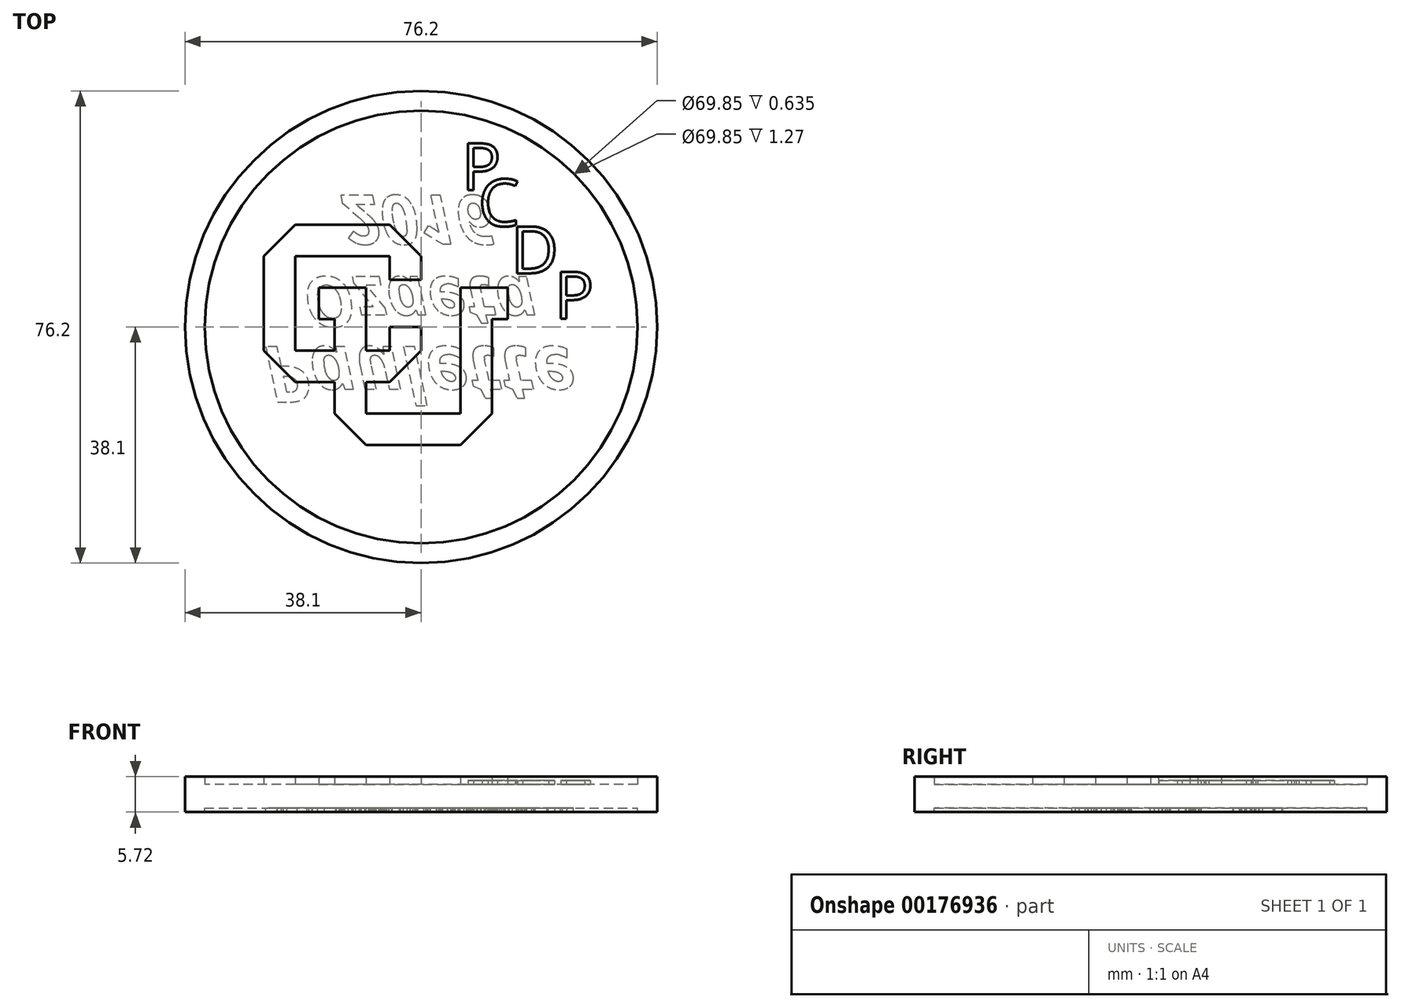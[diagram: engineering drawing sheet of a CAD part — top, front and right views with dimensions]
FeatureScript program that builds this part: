
annotation { "Feature Type Name" : "Feature", "Feature Type Description" : "" }
export const myFeature = defineFeature(function(context is Context, id is Id, definition is map)
    precondition{}
    {
        {
            var Q0;
            Q0=qCreatedBy(makeId("Top.planeOp"),FACE);
            var sketch = newSketch(context, id + "F0", { "sketchPlane" : qUnion([Q0])});
            skCircle(sketch, "E0", {"center": v(0, 0) * mm, "radius": 38.1 * mm});
            skSolve(sketch);
        }
        {
            var Q0;
            Q0=qCreatedBy(makeId("Top.planeOp"),FACE);
            var sketch = newSketch(context, id + "F1", { "sketchPlane" : qUnion([Q0])});
            skCircle(sketch, "E1", {"center": v(0, 0) * mm, "radius": 38.1 * mm});
            skLineSegment(sketch, "E2", {"start": v(0, 0) * mm, "end": v(0, -3.81) * mm});
            skLineSegment(sketch, "E3", {"start": v(0, -3.81) * mm, "end": v(-5.08, -8.9) * mm});
            skLineSegment(sketch, "E4", {"start": v(-5.08, -8.9) * mm, "end": v(-8.89, -8.9) * mm});
            skLineSegment(sketch, "E5", {"start": v(-20.32, -8.9) * mm, "end": v(-25.4, -3.81) * mm});
            skLineSegment(sketch, "E6", {"start": v(-25.4, -3.81) * mm, "end": v(-25.4, 11.43) * mm});
            skLineSegment(sketch, "E7", {"start": v(-25.4, 11.43) * mm, "end": v(-20.32, 16.5) * mm});
            skLineSegment(sketch, "E8", {"start": v(-20.32, 16.5) * mm, "end": v(-5.08, 16.5) * mm});
            skLineSegment(sketch, "E9", {"start": v(-5.08, 16.5) * mm, "end": v(0, 11.43) * mm});
            skLineSegment(sketch, "E10", {"start": v(0, 11.43) * mm, "end": v(0, 7.62) * mm});
            skLineSegment(sketch, "E11", {"start": v(0, 7.62) * mm, "end": v(-5.08, 7.62) * mm});
            skLineSegment(sketch, "E12", {"start": v(-5.08, 7.62) * mm, "end": v(-5.08, 11.43) * mm});
            skLineSegment(sketch, "E13", {"start": v(-5.08, 11.43) * mm, "end": v(-20.32, 11.43) * mm});
            skLineSegment(sketch, "E14", {"start": v(-20.32, 11.43) * mm, "end": v(-20.32, -3.81) * mm});
            skLineSegment(sketch, "E15", {"start": v(-20.32, -3.81) * mm, "end": v(-13.97, -3.81) * mm});
            skLineSegment(sketch, "E16", {"start": v(-5.08, -3.81) * mm, "end": v(-5.08, 0) * mm});
            skLineSegment(sketch, "E17", {"start": v(-5.08, 0) * mm, "end": v(0, 0) * mm});
            skLineSegment(sketch, "E18", {"start": v(-8.89, -3.81) * mm, "end": v(-8.89, 6.35) * mm});
            skLineSegment(sketch, "E19", {"start": v(-8.89, 6.35) * mm, "end": v(-16.51, 6.35) * mm});
            skLineSegment(sketch, "E20", {"start": v(-16.51, 6.35) * mm, "end": v(-16.51, 1.27) * mm});
            skLineSegment(sketch, "E21", {"start": v(-16.51, 1.27) * mm, "end": v(-13.97, 1.27) * mm});
            skLineSegment(sketch, "E22", {"start": v(-13.97, 1.27) * mm, "end": v(-13.97, -3.81) * mm});
            skLineSegment(sketch, "E23.trimOffspring", {"start": v(-8.89, -3.81) * mm, "end": v(-5.08, -3.81) * mm});
            skLineSegment(sketch, "E24", {"start": v(-13.97, -8.9) * mm, "end": v(-13.97, -13.97) * mm});
            skLineSegment(sketch, "E25", {"start": v(-13.97, -13.97) * mm, "end": v(-8.89, -19.05) * mm});
            skLineSegment(sketch, "E26", {"start": v(-8.89, -19.05) * mm, "end": v(6.35, -19.05) * mm});
            skLineSegment(sketch, "E27", {"start": v(6.35, -19.05) * mm, "end": v(11.43, -13.97) * mm});
            skLineSegment(sketch, "E28", {"start": v(6.35, 6.35) * mm, "end": v(6.35, -13.97) * mm});
            skLineSegment(sketch, "E29.trimOffspring", {"start": v(-13.97, -8.9) * mm, "end": v(-20.32, -8.9) * mm});
            skCircle(sketch, "E30", {"center": v(0, 0) * mm, "radius": 34.93 * mm});
            skPoint(sketch, "E31.orphan", {"position": v(6.35, -3.8) * mm});
            skLineSegment(sketch, "E32", {"start": v(6.35, 6.35) * mm, "end": v(13.97, 6.35) * mm});
            skLineSegment(sketch, "E33", {"start": v(13.97, 6.35) * mm, "end": v(13.97, 1.27) * mm});
            skLineSegment(sketch, "E34", {"start": v(11.43, -13.97) * mm, "end": v(11.43, 1.27) * mm});
            skLineSegment(sketch, "E35", {"start": v(11.43, 1.27) * mm, "end": v(13.97, 1.27) * mm});
            skLineSegment(sketch, "E36", {"start": v(6.35, -13.97) * mm, "end": v(-8.89, -13.97) * mm});
            skLineSegment(sketch, "E37", {"start": v(-8.89, -13.97) * mm, "end": v(-8.89, -8.9) * mm});
            skText(sketch, "E38", { "text": "P", "fontName": "OpenSans-Regular.ttf"});
            skText(sketch, "E39", { "text": "C\n", "fontName": "OpenSans-Regular.ttf"});
            skText(sketch, "E40", { "text": "D", "fontName": "OpenSans-Regular.ttf"});
            skText(sketch, "E41", { "text": "P\n", "fontName": "OpenSans-Regular.ttf"});
            const initialGuessF1  = {"E38": [0.00651, 0.0221, 1, 0, 0.00762], "E39": [0.00922, 0.01628, 1, 0, 0.00762], "E40": [0.01445, 0.00866, 1, 0, 0.00762], "E41": [0.0215, 0.00136, 1, 0, 0.00762]};
            skSetInitialGuess(sketch, initialGuessF1);
            skSolve(sketch);
        }
        {
            var Q0;
            Q0 = qSketchRegion(id + "F0", true);
            extrude(context, id + "F2", {"entities" : qUnion([Q0]), "oppositeDirection" : true, "depth" : 3.8 * mm});
        }
        {
            var Q0;
            Q0=makeQuery(id+"F1.imprint","IMPRINT",FACE,{"disambiguationData":[TD([[makeQuery(id+"F1.imprint","IMPRINT",EDGE,{"derivedFrom":sQuery(id+"F1.wireOp",EDGE,"E2")}),-1.0]])]});
            var Q1;
            Q1=makeQuery(id+"F1.imprint","IMPRINT",FACE,{"disambiguationData":[TD([[makeQuery(id+"F1.imprint","IMPRINT",EDGE,{"derivedFrom":sQuery(id+"F1.wireOp",EDGE,"E1")}),1.0]])]});
            var Q2;
            Q2=makeQuery(id+"F1.imprint","IMPRINT",FACE,{"disambiguationData":[TD([[makeQuery(id+"F1.imprint","IMPRINT",EDGE,{"derivedFrom":sQuery(id+"F1.wireOp",EDGE,"E38.sketch_text.stroke-0")}),-1.0]])]});
            var Q3;
            Q3=makeQuery(id+"F1.imprint","IMPRINT",FACE,{"disambiguationData":[TD([[makeQuery(id+"F1.imprint","IMPRINT",EDGE,{"derivedFrom":sQuery(id+"F1.wireOp",EDGE,"E39.sketch_text.stroke-0")}),-1.0]])]});
            var Q4;
            Q4=makeQuery(id+"F1.imprint","IMPRINT",FACE,{"disambiguationData":[TD([[makeQuery(id+"F1.imprint","IMPRINT",EDGE,{"derivedFrom":sQuery(id+"F1.wireOp",EDGE,"E40.sketch_text.stroke-0")}),-1.0]])]});
            var Q5;
            Q5=makeQuery(id+"F1.imprint","IMPRINT",FACE,{"disambiguationData":[TD([[makeQuery(id+"F1.imprint","IMPRINT",EDGE,{"derivedFrom":sQuery(id+"F1.wireOp",EDGE,"E41.sketch_text.stroke-0")}),-1.0]])]});
            extrude(context, id + "F3", {"entities" : qUnion([Q0, Q1, Q2, Q3, Q4, Q5]), "operationType" : NewBodyOperationType.ADD, "depth" : 0.64 * mm});
        }
        {
            var Q0;
            Q0=makeQuery(id+"F2.opExtrude","CAP_FACE",FACE,{"disambiguationData":[OSD([sQuery(id+"F0.wireOp",EDGE,"E0")])],"isStart":false});
            var sketch = newSketch(context, id + "F4", { "sketchPlane" : qUnion([Q0])});
            skText(sketch, "E42", { "text": "Paulette", "fontName": "OpenSans-BoldItalic.ttf"});
            skText(sketch, "E43", { "text": "Ozaeta", "fontName": "OpenSans-BoldItalic.ttf"});
            skText(sketch, "E44", { "text": "2016", "fontName": "OpenSans-BoldItalic.ttf"});
            skCircle(sketch, "E45", {"center": v(0, 0) * mm, "radius": 34.93 * mm});
            const initialGuessF4  = {"E42": [-0.0254, 0.00317, 1, 0, 0.00903], "E43": [-0.01905, -0.0081, 1, 0, 0.0081], "E44": [-0.0127, -0.02124, 1, 0, 0.00794]};
            skSetInitialGuess(sketch, initialGuessF4);
            skSolve(sketch);
        }
        {
            var Q0;
            Q0=makeQuery(id+"F4.imprint","IMPRINT",FACE,{"disambiguationData":[TD([[makeQuery(id+"F4.imprint","IMPRINT",EDGE,{"derivedFrom":sQuery(id+"F4.wireOp",EDGE,"E42.sketch_text.stroke-85")}),-1.0]])]});
            var Q1;
            Q1=makeQuery(id+"F4.imprint","IMPRINT",FACE,{"disambiguationData":[TD([[makeQuery(id+"F4.imprint","IMPRINT",EDGE,{"derivedFrom":sQuery(id+"F4.wireOp",EDGE,"E42.sketch_text.stroke-104")}),-1.0]])]});
            var Q2;
            Q2=makeQuery(id+"F4.imprint","IMPRINT",FACE,{"disambiguationData":[TD([[makeQuery(id+"F4.imprint","IMPRINT",EDGE,{"derivedFrom":sQuery(id+"F4.wireOp",EDGE,"E42.sketch_text.stroke-123")}),-1.0]])]});
            var Q3;
            Q3=makeQuery(id+"F4.imprint","IMPRINT",FACE,{"disambiguationData":[TD([[makeQuery(id+"F4.imprint","IMPRINT",EDGE,{"derivedFrom":sQuery(id+"F4.wireOp",EDGE,"E42.sketch_text.stroke-61")}),-1.0]])]});
            var Q4;
            Q4=makeQuery(id+"F4.imprint","IMPRINT",FACE,{"disambiguationData":[TD([[makeQuery(id+"F4.imprint","IMPRINT",EDGE,{"derivedFrom":sQuery(id+"F4.wireOp",EDGE,"E42.sketch_text.stroke-57")}),-1.0]])]});
            var Q5;
            Q5=makeQuery(id+"F4.imprint","IMPRINT",FACE,{"disambiguationData":[TD([[makeQuery(id+"F4.imprint","IMPRINT",EDGE,{"derivedFrom":sQuery(id+"F4.wireOp",EDGE,"E42.sketch_text.stroke-40")}),-1.0]])]});
            var Q6;
            Q6=makeQuery(id+"F4.imprint","IMPRINT",FACE,{"disambiguationData":[TD([[makeQuery(id+"F4.imprint","IMPRINT",EDGE,{"derivedFrom":sQuery(id+"F4.wireOp",EDGE,"E42.sketch_text.stroke-15")}),-1.0]])]});
            var Q7;
            Q7=makeQuery(id+"F4.imprint","IMPRINT",FACE,{"disambiguationData":[TD([[makeQuery(id+"F4.imprint","IMPRINT",EDGE,{"derivedFrom":sQuery(id+"F4.wireOp",EDGE,"E42.sketch_text.stroke-0")}),-1.0]])]});
            var Q8;
            Q8=makeQuery(id+"F4.imprint","IMPRINT",FACE,{"disambiguationData":[TD([[makeQuery(id+"F4.imprint","IMPRINT",EDGE,{"derivedFrom":sQuery(id+"F4.wireOp",EDGE,"E43.sketch_text.stroke-0")}),-1.0]])]});
            var Q9;
            Q9=makeQuery(id+"F4.imprint","IMPRINT",FACE,{"disambiguationData":[TD([[makeQuery(id+"F4.imprint","IMPRINT",EDGE,{"derivedFrom":sQuery(id+"F4.wireOp",EDGE,"E43.sketch_text.stroke-20")}),-1.0]])]});
            var Q10;
            Q10=makeQuery(id+"F4.imprint","IMPRINT",FACE,{"disambiguationData":[TD([[makeQuery(id+"F4.imprint","IMPRINT",EDGE,{"derivedFrom":sQuery(id+"F4.wireOp",EDGE,"E43.sketch_text.stroke-30")}),-1.0]])]});
            var Q11;
            Q11=makeQuery(id+"F4.imprint","IMPRINT",FACE,{"disambiguationData":[TD([[makeQuery(id+"F4.imprint","IMPRINT",EDGE,{"derivedFrom":sQuery(id+"F4.wireOp",EDGE,"E43.sketch_text.stroke-55")}),-1.0]])]});
            var Q12;
            Q12=makeQuery(id+"F4.imprint","IMPRINT",FACE,{"disambiguationData":[TD([[makeQuery(id+"F4.imprint","IMPRINT",EDGE,{"derivedFrom":sQuery(id+"F4.wireOp",EDGE,"E43.sketch_text.stroke-79")}),-1.0]])]});
            var Q13;
            Q13=makeQuery(id+"F4.imprint","IMPRINT",FACE,{"disambiguationData":[TD([[makeQuery(id+"F4.imprint","IMPRINT",EDGE,{"derivedFrom":sQuery(id+"F4.wireOp",EDGE,"E43.sketch_text.stroke-98")}),-1.0]])]});
            var Q14;
            Q14=makeQuery(id+"F4.imprint","IMPRINT",FACE,{"disambiguationData":[TD([[makeQuery(id+"F4.imprint","IMPRINT",EDGE,{"derivedFrom":sQuery(id+"F4.wireOp",EDGE,"E44.sketch_text.stroke-48")}),-1.0]])]});
            var Q15;
            Q15=makeQuery(id+"F4.imprint","IMPRINT",FACE,{"disambiguationData":[TD([[makeQuery(id+"F4.imprint","IMPRINT",EDGE,{"derivedFrom":sQuery(id+"F4.wireOp",EDGE,"E44.sketch_text.stroke-39")}),-1.0]])]});
            var Q16;
            Q16=makeQuery(id+"F4.imprint","IMPRINT",FACE,{"disambiguationData":[TD([[makeQuery(id+"F4.imprint","IMPRINT",EDGE,{"derivedFrom":sQuery(id+"F4.wireOp",EDGE,"E44.sketch_text.stroke-21")}),-1.0]])]});
            var Q17;
            Q17=makeQuery(id+"F4.imprint","IMPRINT",FACE,{"disambiguationData":[TD([[makeQuery(id+"F4.imprint","IMPRINT",EDGE,{"derivedFrom":sQuery(id+"F4.wireOp",EDGE,"E44.sketch_text.stroke-0")}),-1.0]])]});
            var Q18;
            Q18=makeQuery(id+"F4.imprint","IMPRINT",FACE,{"disambiguationData":[TD([[makeQuery(id+"F4.imprint","IMPRINT",EDGE,{"derivedFrom":sQuery(id+"F4.wireOp",EDGE,"E45")}),-1.0]])]});
            var Q19;
            Q19 = qSketchRegion(id + "F1", true);
            extrude(context, id + "F5", {"entities" : qUnion([Q0, Q1, Q2, Q3, Q4, Q5, Q6, Q7, Q8, Q9, Q10, Q11, Q12, Q13, Q14, Q15, Q16, Q17, Q18, Q19]), "operationType" : NewBodyOperationType.ADD, "depth" : 0.64 * mm});
        }
        {
            var Q0;
            Q0 = qSketchRegion(id + "F0", true);
            extrude(context, id + "F6", {"entities" : qUnion([Q0]), "operationType" : NewBodyOperationType.ADD, "oppositeDirection" : true, "depth" : 0.64 * mm});
        }
        {
            var Q0;
            Q0 = qSketchRegion(id + "F1", true);
            var Q1;
            Q1=makeQuery(id+"F3.opExtrude","CAP_FACE",FACE,{"disambiguationData":[OSD([sQuery(id+"F1.wireOp",EDGE,"E2"),sQuery(id+"F1.wireOp",EDGE,"E3"),sQuery(id+"F1.wireOp",EDGE,"E4"),sQuery(id+"F1.wireOp",EDGE,"E5"),sQuery(id+"F1.wireOp",EDGE,"E6"),sQuery(id+"F1.wireOp",EDGE,"E7"),sQuery(id+"F1.wireOp",EDGE,"E8"),sQuery(id+"F1.wireOp",EDGE,"E9"),sQuery(id+"F1.wireOp",EDGE,"E10"),sQuery(id+"F1.wireOp",EDGE,"E11"),sQuery(id+"F1.wireOp",EDGE,"E12"),sQuery(id+"F1.wireOp",EDGE,"E13"),sQuery(id+"F1.wireOp",EDGE,"E14"),sQuery(id+"F1.wireOp",EDGE,"E15"),sQuery(id+"F1.wireOp",EDGE,"E16"),sQuery(id+"F1.wireOp",EDGE,"E17"),sQuery(id+"F1.wireOp",EDGE,"E18"),sQuery(id+"F1.wireOp",EDGE,"E19"),sQuery(id+"F1.wireOp",EDGE,"E20"),sQuery(id+"F1.wireOp",EDGE,"E21"),sQuery(id+"F1.wireOp",EDGE,"E22"),sQuery(id+"F1.wireOp",EDGE,"E23.trimOffspring"),sQuery(id+"F1.wireOp",EDGE,"E24"),sQuery(id+"F1.wireOp",EDGE,"E25"),sQuery(id+"F1.wireOp",EDGE,"E26"),sQuery(id+"F1.wireOp",EDGE,"E27"),sQuery(id+"F1.wireOp",EDGE,"E28"),sQuery(id+"F1.wireOp",EDGE,"E29.trimOffspring"),sQuery(id+"F1.wireOp",EDGE,"E32"),sQuery(id+"F1.wireOp",EDGE,"E33"),sQuery(id+"F1.wireOp",EDGE,"E34"),sQuery(id+"F1.wireOp",EDGE,"E35"),sQuery(id+"F1.wireOp",EDGE,"E36"),sQuery(id+"F1.wireOp",EDGE,"E37")])],"isStart":false});
            var Q2;
            Q2=makeQuery(id+"F3.opExtrude","CAP_FACE",FACE,{"disambiguationData":[OSD([sQuery(id+"F1.wireOp",EDGE,"E1"),sQuery(id+"F1.wireOp",EDGE,"E30")])],"isStart":false});
            extrude(context, id + "F7", {"entities" : qUnion([Q0, Q1, Q2]), "operationType" : NewBodyOperationType.ADD, "depth" : 0.64 * mm});
        }
    });
